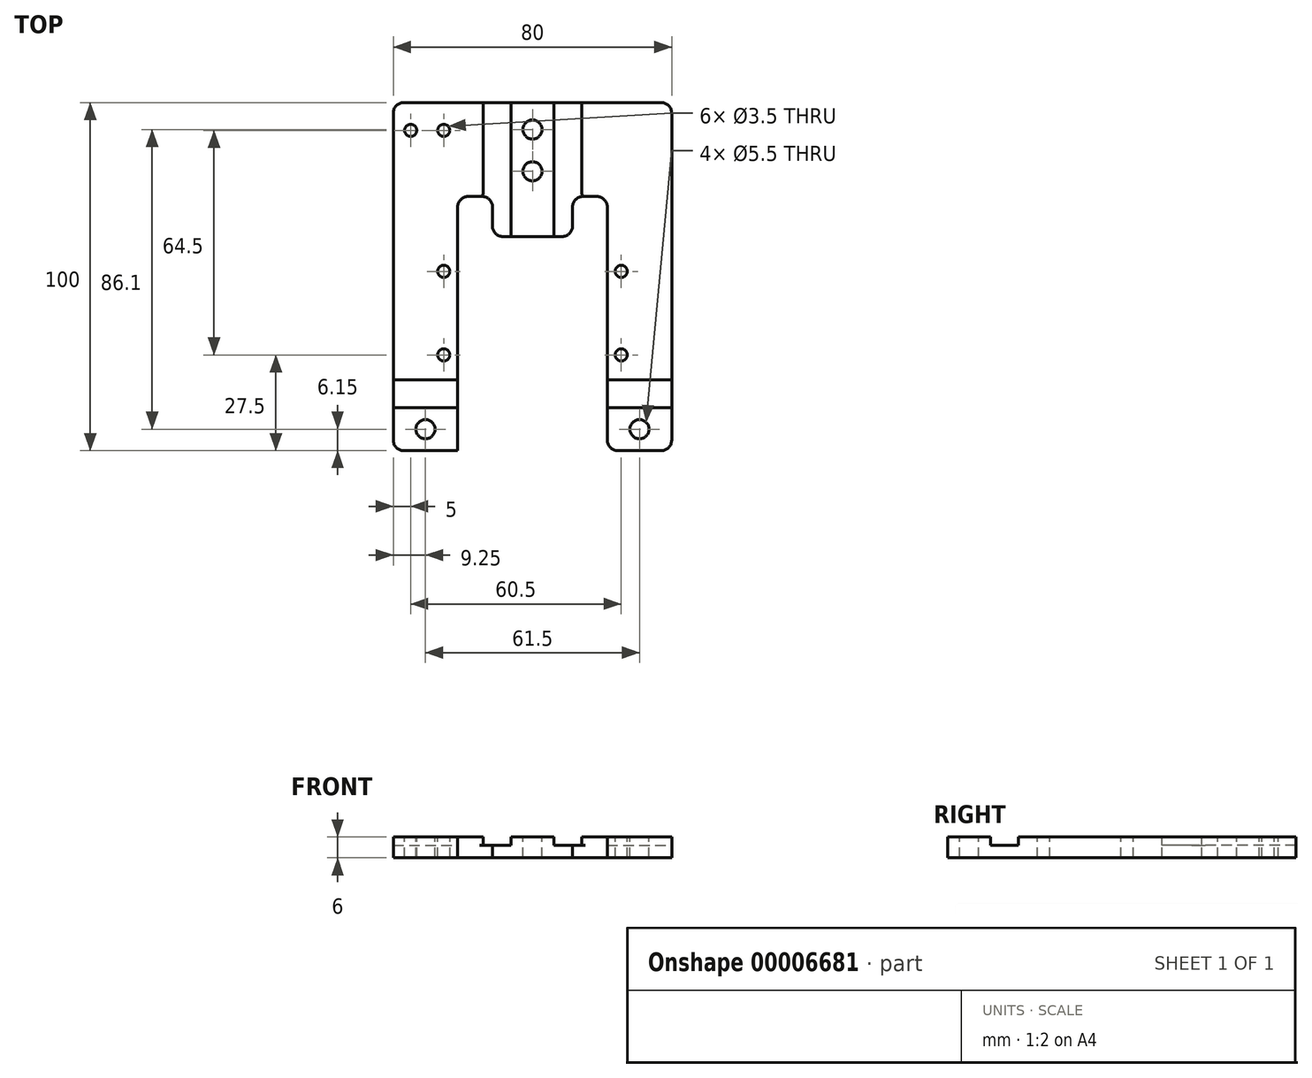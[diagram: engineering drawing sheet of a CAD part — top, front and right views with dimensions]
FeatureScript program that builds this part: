
annotation { "Feature Type Name" : "Feature", "Feature Type Description" : "" }
export const myFeature = defineFeature(function(context is Context, id is Id, definition is map)
    precondition{}
    {
        {
            var Q0;
            Q0=qCreatedBy(makeId("Top.planeOp"),FACE);
            var sketch = newSketch(context, id + "F0", { "sketchPlane" : qUnion([Q0])});
            skLineSegment(sketch, "E0.bottom", {"start": v(0, 0) * mm, "end": v(80, 0) * mm});
            skLineSegment(sketch, "E0.top", {"start": v(0, 100) * mm, "end": v(80, 100) * mm});
            skLineSegment(sketch, "E0.left", {"start": v(0, 0) * mm, "end": v(0, 100) * mm});
            skLineSegment(sketch, "E0.right", {"start": v(80, 0) * mm, "end": v(80, 100) * mm});
            skSolve(sketch);
        }
        {
            var Q0;
            Q0 = qSketchRegion(id + "F0", true);
            extrude(context, id + "F1", {"entities" : qUnion([Q0]), "depth" : 6 * mm});
        }
        {
            var Q0;
            Q0=makeQuery(id+"F1.opExtrude","CAP_FACE",FACE,{"disambiguationData":[OSD([sQuery(id+"F0.wireOp",EDGE,"E0.bottom"),sQuery(id+"F0.wireOp",EDGE,"E0.top"),sQuery(id+"F0.wireOp",EDGE,"E0.left"),sQuery(id+"F0.wireOp",EDGE,"E0.right")])],"isStart":false});
            var sketch = newSketch(context, id + "F2", { "sketchPlane" : qUnion([Q0])});
            skLineSegment(sketch, "E1.bottom", {"start": v(18.5, 0) * mm, "end": v(61.5, 0) * mm});
            skLineSegment(sketch, "E1.top", {"start": v(28.5, 61.5) * mm, "end": v(51.5, 61.5) * mm});
            skLineSegment(sketch, "E1.left", {"start": v(18.5, 0) * mm, "end": v(18.5, 61.5) * mm});
            skLineSegment(sketch, "E1.right", {"start": v(61.5, 0) * mm, "end": v(61.5, 61.5) * mm});
            skLineSegment(sketch, "E2.top", {"start": v(18.5, 73) * mm, "end": v(28.5, 73) * mm});
            skLineSegment(sketch, "E2.left", {"start": v(18.5, 61.5) * mm, "end": v(18.5, 73) * mm});
            skLineSegment(sketch, "E2.right", {"start": v(28.5, 61.5) * mm, "end": v(28.5, 73) * mm});
            skLineSegment(sketch, "E3.top", {"start": v(61.5, 73) * mm, "end": v(51.5, 73) * mm});
            skLineSegment(sketch, "E3.left", {"start": v(61.5, 61.5) * mm, "end": v(61.5, 73) * mm});
            skLineSegment(sketch, "E3.right", {"start": v(51.5, 61.5) * mm, "end": v(51.5, 73) * mm});
            skSolve(sketch);
        }
        {
            var Q0;
            Q0 = qSketchRegion(id + "F2", true);
            extrude(context, id + "F3", {"entities" : qUnion([Q0]), "operationType" : NewBodyOperationType.REMOVE, "endBound" : BoundingType.THROUGH_ALL, "oppositeDirection" : true, "depth" : 25 * mm});
        }
        {
            var Q0;
            Q0=makeQuery(id+"F1.opExtrude","CAP_FACE",FACE,{"disambiguationData":[OSD([sQuery(id+"F0.wireOp",EDGE,"E0.bottom"),sQuery(id+"F0.wireOp",EDGE,"E0.top"),sQuery(id+"F0.wireOp",EDGE,"E0.left"),sQuery(id+"F0.wireOp",EDGE,"E0.right")])],"isStart":false});
            var sketch = newSketch(context, id + "F4", { "sketchPlane" : qUnion([Q0])});
            skLineSegment(sketch, "E4", {"start": v(0, 12.3) * mm, "end": v(18.5, 12.3) * mm});
            skLineSegment(sketch, "E5", {"start": v(61.5, 12.3) * mm, "end": v(80, 12.3) * mm});
            skLineSegment(sketch, "E6.0", {"start": v(46.15, 100) * mm, "end": v(46.15, 61.5) * mm});
            skLineSegment(sketch, "E7.0", {"start": v(33.85, 100) * mm, "end": v(33.85, 61.5) * mm});
            skLineSegment(sketch, "E8.0", {"start": v(25.85, 100) * mm, "end": v(25.85, 61.5) * mm});
            skLineSegment(sketch, "E9.0", {"start": v(54.15, 100) * mm, "end": v(54.15, 61.5) * mm});
            skLineSegment(sketch, "E10.0", {"start": v(61.5, 20.3) * mm, "end": v(80, 20.3) * mm});
            skLineSegment(sketch, "E11.0", {"start": v(0, 20.3) * mm, "end": v(18.5, 20.3) * mm});
            skLineSegment(sketch, "E12", {"start": v(25.85, 100) * mm, "end": v(33.85, 100) * mm});
            skLineSegment(sketch, "E13", {"start": v(46.15, 100) * mm, "end": v(54.15, 100) * mm});
            skLineSegment(sketch, "E14", {"start": v(54.15, 61.5) * mm, "end": v(46.15, 61.5) * mm});
            skLineSegment(sketch, "E15", {"start": v(33.85, 61.5) * mm, "end": v(25.85, 61.5) * mm});
            skLineSegment(sketch, "E16", {"start": v(0, 20.3) * mm, "end": v(0, 12.3) * mm});
            skLineSegment(sketch, "E17", {"start": v(18.5, 12.3) * mm, "end": v(18.5, 20.3) * mm});
            skLineSegment(sketch, "E18", {"start": v(61.5, 20.3) * mm, "end": v(61.5, 12.3) * mm});
            skLineSegment(sketch, "E19", {"start": v(80, 12.3) * mm, "end": v(80, 20.3) * mm});
            skLineSegment(sketch, "E20", {"start": v(40, 100) * mm, "end": v(40, 61.5) * mm, "construction": true});
            skSolve(sketch);
        }
        {
            var Q0;
            Q0 = qSketchRegion(id + "F4", true);
            extrude(context, id + "F5", {"entities" : qUnion([Q0]), "operationType" : NewBodyOperationType.REMOVE, "oppositeDirection" : true, "depth" : 2.4 * mm});
        }
        {
            var Q0;
            {var subQ0=sQuery(id+"F0.wireOp",EDGE,"E0.top");Q0=makeQuery(id+"F5.boolean.opBoolean","SPLIT",FACE,{"disambiguationData":[TD([makeQuery(id+"F3.boolean.opBoolean","COPY",FACE,{"derivedFrom":makeQuery(id+"F3.opExtrude","SWEPT_FACE",FACE,{"disambiguationData":[OSD([sQuery(id+"F2.wireOp",EDGE,"E1.top")])]})})])],"derivedFrom":makeQuery(id+"F1.opExtrude","CAP_FACE",FACE,{"disambiguationData":[OSD([sQuery(id+"F0.wireOp",EDGE,"E0.bottom"),subQ0,sQuery(id+"F0.wireOp",EDGE,"E0.left"),sQuery(id+"F0.wireOp",EDGE,"E0.right")])],"isStart":false})});}
            var sketch = newSketch(context, id + "F6", { "sketchPlane" : qUnion([Q0])});
            skLineSegment(sketch, "E21", {"start": v(40, 100) * mm, "end": v(40, 61.5) * mm});
            skCircle(sketch, "E22", {"center": v(40, 92.25) * mm, "radius": 2.75 * mm});
            skCircle(sketch, "E23", {"center": v(40, 80.25) * mm, "radius": 2.75 * mm});
            skSolve(sketch);
        }
        {
            var Q0;
            Q0 = qSketchRegion(id + "F6", true);
            extrude(context, id + "F7", {"entities" : qUnion([Q0]), "operationType" : NewBodyOperationType.REMOVE, "endBound" : BoundingType.THROUGH_ALL, "oppositeDirection" : true, "depth" : 25 * mm});
        }
        {
            var Q0;
            {var subQ0=sQuery(id+"F0.wireOp",EDGE,"E0.bottom");var subQ1=sQuery(id+"F0.wireOp",EDGE,"E0.left");Q0=makeQuery(id+"F5.boolean.opBoolean","SPLIT",FACE,{"disambiguationData":[TD([makeQuery(id+"F5.opExtrude","SWEPT_FACE",FACE,{"disambiguationData":[OSD([sQuery(id+"F4.wireOp",EDGE,"E4")])]})])],"derivedFrom":makeQuery(id+"F1.opExtrude","CAP_FACE",FACE,{"disambiguationData":[OSD([subQ0,sQuery(id+"F0.wireOp",EDGE,"E0.top"),subQ1,sQuery(id+"F0.wireOp",EDGE,"E0.right")])],"isStart":false})});}
            var sketch = newSketch(context, id + "F8", { "sketchPlane" : qUnion([Q0])});
            skLineSegment(sketch, "E24", {"start": v(9.25, 12.3) * mm, "end": v(9.25, 0) * mm, "construction": true});
            skCircle(sketch, "E25", {"center": v(9.25, 6.15) * mm, "radius": 2.75 * mm});
            skSolve(sketch);
        }
        {
            var Q0;
            Q0 = qSketchRegion(id + "F8", true);
            extrude(context, id + "F9", {"entities" : qUnion([Q0]), "operationType" : NewBodyOperationType.REMOVE, "endBound" : BoundingType.THROUGH_ALL, "oppositeDirection" : true, "depth" : 25 * mm});
        }
        {
            var Q0;
            {var subQ0=sQuery(id+"F0.wireOp",EDGE,"E0.bottom");var subQ1=sQuery(id+"F0.wireOp",EDGE,"E0.right");Q0=makeQuery(id+"F5.boolean.opBoolean","SPLIT",FACE,{"disambiguationData":[TD([makeQuery(id+"F5.opExtrude","SWEPT_FACE",FACE,{"disambiguationData":[OSD([sQuery(id+"F4.wireOp",EDGE,"E5")])]})])],"derivedFrom":makeQuery(id+"F1.opExtrude","CAP_FACE",FACE,{"disambiguationData":[OSD([subQ0,sQuery(id+"F0.wireOp",EDGE,"E0.top"),sQuery(id+"F0.wireOp",EDGE,"E0.left"),subQ1])],"isStart":false})});}
            var sketch = newSketch(context, id + "F10", { "sketchPlane" : qUnion([Q0])});
            skLineSegment(sketch, "E26", {"start": v(70.75, 12.3) * mm, "end": v(70.75, 0) * mm, "construction": true});
            skCircle(sketch, "E27", {"center": v(70.75, 6.15) * mm, "radius": 2.75 * mm});
            skSolve(sketch);
        }
        {
            var Q0;
            Q0 = qSketchRegion(id + "F10", true);
            extrude(context, id + "F11", {"entities" : qUnion([Q0]), "operationType" : NewBodyOperationType.REMOVE, "endBound" : BoundingType.THROUGH_ALL, "oppositeDirection" : true, "depth" : 25 * mm});
        }
        {
            var Q0;
            {var subQ0=sQuery(id+"F0.wireOp",EDGE,"E0.top");var subQ1=sQuery(id+"F0.wireOp",EDGE,"E0.left");Q0=makeQuery(id+"F5.boolean.opBoolean","SPLIT",FACE,{"disambiguationData":[TD([makeQuery(id+"F3.boolean.opBoolean","COPY",FACE,{"derivedFrom":makeQuery(id+"F3.opExtrude","SWEPT_FACE",FACE,{"disambiguationData":[OSD([sQuery(id+"F2.wireOp",EDGE,"E2.top")])]})})])],"derivedFrom":makeQuery(id+"F1.opExtrude","CAP_FACE",FACE,{"disambiguationData":[OSD([sQuery(id+"F0.wireOp",EDGE,"E0.bottom"),subQ0,subQ1,sQuery(id+"F0.wireOp",EDGE,"E0.right")])],"isStart":false})});}
            var sketch = newSketch(context, id + "F12", { "sketchPlane" : qUnion([Q0])});
            skLineSegment(sketch, "E28", {"start": v(0, 92) * mm, "end": v(25.85, 92) * mm, "construction": true});
            skCircle(sketch, "E29", {"center": v(5, 92) * mm, "radius": 1.75 * mm});
            skCircle(sketch, "E30", {"center": v(14.5, 92) * mm, "radius": 1.75 * mm});
            skSolve(sketch);
        }
        {
            var Q0;
            Q0 = qSketchRegion(id + "F12", true);
            extrude(context, id + "F13", {"entities" : qUnion([Q0]), "operationType" : NewBodyOperationType.REMOVE, "endBound" : BoundingType.THROUGH_ALL, "oppositeDirection" : true, "depth" : 25 * mm});
        }
        {
            var Q0;
            {var subQ0=sQuery(id+"F0.wireOp",EDGE,"E0.top");var subQ1=sQuery(id+"F0.wireOp",EDGE,"E0.left");Q0=makeQuery(id+"F5.boolean.opBoolean","SPLIT",FACE,{"disambiguationData":[TD([makeQuery(id+"F3.boolean.opBoolean","COPY",FACE,{"derivedFrom":makeQuery(id+"F3.opExtrude","SWEPT_FACE",FACE,{"disambiguationData":[OSD([sQuery(id+"F2.wireOp",EDGE,"E2.top")])]})})])],"derivedFrom":makeQuery(id+"F1.opExtrude","CAP_FACE",FACE,{"disambiguationData":[OSD([sQuery(id+"F0.wireOp",EDGE,"E0.bottom"),subQ0,subQ1,sQuery(id+"F0.wireOp",EDGE,"E0.right")])],"isStart":false})});}
            var sketch = newSketch(context, id + "F14", { "sketchPlane" : qUnion([Q0])});
            skLineSegment(sketch, "E31", {"start": v(14.5, 20.3) * mm, "end": v(14.5, 73) * mm, "construction": true});
            skCircle(sketch, "E32", {"center": v(14.5, 51.5) * mm, "radius": 1.75 * mm});
            skCircle(sketch, "E33", {"center": v(14.5, 27.5) * mm, "radius": 1.75 * mm});
            skSolve(sketch);
        }
        {
            var Q0;
            Q0 = qSketchRegion(id + "F14", true);
            extrude(context, id + "F15", {"entities" : qUnion([Q0]), "operationType" : NewBodyOperationType.REMOVE, "endBound" : BoundingType.THROUGH_ALL, "oppositeDirection" : true, "depth" : 25 * mm});
        }
        {
            var Q0;
            {var subQ0=sQuery(id+"F0.wireOp",EDGE,"E0.top");var subQ1=sQuery(id+"F0.wireOp",EDGE,"E0.right");Q0=makeQuery(id+"F5.boolean.opBoolean","SPLIT",FACE,{"disambiguationData":[TD([makeQuery(id+"F3.boolean.opBoolean","COPY",FACE,{"derivedFrom":makeQuery(id+"F3.opExtrude","SWEPT_FACE",FACE,{"disambiguationData":[OSD([sQuery(id+"F2.wireOp",EDGE,"E3.top")])]})})])],"derivedFrom":makeQuery(id+"F1.opExtrude","CAP_FACE",FACE,{"disambiguationData":[OSD([sQuery(id+"F0.wireOp",EDGE,"E0.bottom"),subQ0,sQuery(id+"F0.wireOp",EDGE,"E0.left"),subQ1])],"isStart":false})});}
            var sketch = newSketch(context, id + "F16", { "sketchPlane" : qUnion([Q0])});
            skLineSegment(sketch, "E34", {"start": v(65.5, 20.3) * mm, "end": v(65.5, 51.38) * mm, "construction": true});
            skCircle(sketch, "E35", {"center": v(65.5, 51.5) * mm, "radius": 1.75 * mm});
            skCircle(sketch, "E36", {"center": v(65.5, 27.5) * mm, "radius": 1.75 * mm});
            skSolve(sketch);
        }
        {
            var Q0;
            Q0 = qSketchRegion(id + "F16", true);
            extrude(context, id + "F17", {"entities" : qUnion([Q0]), "operationType" : NewBodyOperationType.REMOVE, "endBound" : BoundingType.THROUGH_ALL, "oppositeDirection" : true, "depth" : 25 * mm});
        }
        {
            var Q0;
            Q0=makeQuery(id+"F1.opExtrude","SWEPT_EDGE",EDGE,{"disambiguationData":[OSD([sQuery(id+"F0.wireOp",EDGE,"E0.bottom"),sQuery(id+"F0.wireOp",EDGE,"E0.left")])]});
            var Q1;
            Q1=makeQuery(id+"F1.opExtrude","SWEPT_EDGE",EDGE,{"disambiguationData":[OSD([sQuery(id+"F0.wireOp",EDGE,"E0.bottom"),sQuery(id+"F0.wireOp",EDGE,"E0.right")])]});
            var Q2;
            Q2=makeQuery(id+"F3.boolean.opBoolean","COPY",EDGE,{"derivedFrom":makeQuery(id+"F3.opExtrude","SWEPT_EDGE",EDGE,{"disambiguationData":[OSD([sQuery(id+"F0.wireOp",EDGE,"E0.bottom"),sQuery(id+"F2.wireOp",EDGE,"E1.bottom"),sQuery(id+"F2.wireOp",EDGE,"E1.right")])]})});
            var Q3;
            Q3=makeQuery(id+"F3.boolean.opBoolean","COPY",EDGE,{"derivedFrom":makeQuery(id+"F3.opExtrude","SWEPT_EDGE",EDGE,{"disambiguationData":[OSD([sQuery(id+"F0.wireOp",EDGE,"E0.bottom"),sQuery(id+"F2.wireOp",EDGE,"E1.bottom"),sQuery(id+"F2.wireOp",EDGE,"E1.left")])]})});
            var Q4;
            Q4=makeQuery(id+"F1.opExtrude","SWEPT_EDGE",EDGE,{"disambiguationData":[OSD([sQuery(id+"F0.wireOp",EDGE,"E0.top"),sQuery(id+"F0.wireOp",EDGE,"E0.left")])]});
            var Q5;
            Q5=makeQuery(id+"F1.opExtrude","SWEPT_EDGE",EDGE,{"disambiguationData":[OSD([sQuery(id+"F0.wireOp",EDGE,"E0.top"),sQuery(id+"F0.wireOp",EDGE,"E0.right")])]});
            var Q6;
            Q6=makeQuery(id+"F3.boolean.opBoolean","COPY",EDGE,{"derivedFrom":makeQuery(id+"F3.opExtrude","SWEPT_EDGE",EDGE,{"disambiguationData":[OSD([sQuery(id+"F2.wireOp",EDGE,"E1.top"),sQuery(id+"F2.wireOp",EDGE,"E3.right")])]})});
            var Q7;
            Q7=makeQuery(id+"F3.boolean.opBoolean","COPY",EDGE,{"derivedFrom":makeQuery(id+"F3.opExtrude","SWEPT_EDGE",EDGE,{"disambiguationData":[OSD([sQuery(id+"F2.wireOp",EDGE,"E1.top"),sQuery(id+"F2.wireOp",EDGE,"E2.right")])]})});
            var Q8;
            Q8=makeQuery(id+"F3.boolean.opBoolean","COPY",EDGE,{"derivedFrom":makeQuery(id+"F3.opExtrude","SWEPT_EDGE",EDGE,{"disambiguationData":[OSD([sQuery(id+"F2.wireOp",EDGE,"E3.top"),sQuery(id+"F2.wireOp",EDGE,"E3.left")])]})});
            var Q9;
            Q9=makeQuery(id+"F3.boolean.opBoolean","COPY",EDGE,{"derivedFrom":makeQuery(id+"F3.opExtrude","SWEPT_EDGE",EDGE,{"disambiguationData":[OSD([sQuery(id+"F2.wireOp",EDGE,"E2.top"),sQuery(id+"F2.wireOp",EDGE,"E2.left")])]})});
            var Q10;
            Q10=makeQuery(id+"F3.boolean.opBoolean","COPY",EDGE,{"derivedFrom":makeQuery(id+"F3.opExtrude","SWEPT_EDGE",EDGE,{"disambiguationData":[OSD([sQuery(id+"F2.wireOp",EDGE,"E3.top"),sQuery(id+"F2.wireOp",EDGE,"E3.right")])]})});
            var Q11;
            Q11=makeQuery(id+"F3.boolean.opBoolean","COPY",EDGE,{"derivedFrom":makeQuery(id+"F3.opExtrude","SWEPT_EDGE",EDGE,{"disambiguationData":[OSD([sQuery(id+"F2.wireOp",EDGE,"E2.top"),sQuery(id+"F2.wireOp",EDGE,"E2.right")])]})});
            fillet(context, id + "F18", {"entities" : qUnion([Q0, Q1, Q2, Q3, Q4, Q5, Q6, Q7, Q8, Q9, Q10, Q11]), "radius" : 3 * mm, "tangentPropagation" : true, "allowEdgeOverflow" : false});
        }
        {
            var Q0;
            Q0=makeQuery(id+"F5.boolean.opBoolean","COPY",EDGE,{"derivedFrom":makeQuery(id+"F5.opExtrude","SWEPT_EDGE",EDGE,{"disambiguationData":[OSD([sQuery(id+"F2.wireOp",EDGE,"E1.top"),sQuery(id+"F4.wireOp",EDGE,"E7.0"),sQuery(id+"F4.wireOp",EDGE,"E15")])]})});
            var Q1;
            Q1=makeQuery(id+"F18.opFillet","BLEND_EDGE",EDGE,{"blendedFrom":[makeQuery(id+"F3.boolean.opBoolean","COPY",EDGE,{"derivedFrom":makeQuery(id+"F3.opExtrude","SWEPT_EDGE",EDGE,{"disambiguationData":[OSD([sQuery(id+"F2.wireOp",EDGE,"E3.top"),sQuery(id+"F2.wireOp",EDGE,"E3.right")])]})}),makeQuery(id+"F5.boolean.opBoolean","COPY",FACE,{"derivedFrom":makeQuery(id+"F5.opExtrude","SWEPT_FACE",FACE,{"disambiguationData":[OSD([sQuery(id+"F4.wireOp",EDGE,"E9.0")])]})})],"blendedInto":[makeQuery(id+"F5.boolean.opBoolean","COPY",FACE,{"derivedFrom":makeQuery(id+"F5.opExtrude","SWEPT_FACE",FACE,{"disambiguationData":[OSD([sQuery(id+"F4.wireOp",EDGE,"E9.0")])]})})]});
            var Q2;
            Q2=makeQuery(id+"F5.boolean.opBoolean","COPY",EDGE,{"derivedFrom":makeQuery(id+"F5.opExtrude","SWEPT_EDGE",EDGE,{"disambiguationData":[OSD([sQuery(id+"F2.wireOp",EDGE,"E1.top"),sQuery(id+"F4.wireOp",EDGE,"E6.0"),sQuery(id+"F4.wireOp",EDGE,"E14")])]})});
            var Q3;
            Q3=makeQuery(id+"F18.opFillet","BLEND_EDGE",EDGE,{"blendedFrom":[makeQuery(id+"F3.boolean.opBoolean","COPY",EDGE,{"derivedFrom":makeQuery(id+"F3.opExtrude","SWEPT_EDGE",EDGE,{"disambiguationData":[OSD([sQuery(id+"F2.wireOp",EDGE,"E2.top"),sQuery(id+"F2.wireOp",EDGE,"E2.right")])]})}),makeQuery(id+"F5.boolean.opBoolean","COPY",FACE,{"derivedFrom":makeQuery(id+"F5.opExtrude","SWEPT_FACE",FACE,{"disambiguationData":[OSD([sQuery(id+"F4.wireOp",EDGE,"E8.0")])]})})],"blendedInto":[makeQuery(id+"F5.boolean.opBoolean","COPY",FACE,{"derivedFrom":makeQuery(id+"F5.opExtrude","SWEPT_FACE",FACE,{"disambiguationData":[OSD([sQuery(id+"F4.wireOp",EDGE,"E8.0")])]})})]});
            var Q4;
            Q4=makeQuery(id+"F5.boolean.opBoolean","COPY",EDGE,{"derivedFrom":makeQuery(id+"F5.opExtrude","SWEPT_EDGE",EDGE,{"disambiguationData":[OSD([sQuery(id+"F0.wireOp",EDGE,"E0.top"),sQuery(id+"F4.wireOp",EDGE,"E8.0"),sQuery(id+"F4.wireOp",EDGE,"E12")])]})});
            var Q5;
            Q5=makeQuery(id+"F5.boolean.opBoolean","COPY",EDGE,{"derivedFrom":makeQuery(id+"F5.opExtrude","SWEPT_EDGE",EDGE,{"disambiguationData":[OSD([sQuery(id+"F0.wireOp",EDGE,"E0.top"),sQuery(id+"F4.wireOp",EDGE,"E7.0"),sQuery(id+"F4.wireOp",EDGE,"E12")])]})});
            var Q6;
            Q6=makeQuery(id+"F5.boolean.opBoolean","COPY",EDGE,{"derivedFrom":makeQuery(id+"F5.opExtrude","SWEPT_EDGE",EDGE,{"disambiguationData":[OSD([sQuery(id+"F0.wireOp",EDGE,"E0.top"),sQuery(id+"F4.wireOp",EDGE,"E6.0"),sQuery(id+"F4.wireOp",EDGE,"E13")])]})});
            var Q7;
            Q7=makeQuery(id+"F5.boolean.opBoolean","COPY",EDGE,{"derivedFrom":makeQuery(id+"F5.opExtrude","SWEPT_EDGE",EDGE,{"disambiguationData":[OSD([sQuery(id+"F0.wireOp",EDGE,"E0.top"),sQuery(id+"F4.wireOp",EDGE,"E9.0"),sQuery(id+"F4.wireOp",EDGE,"E13")])]})});
            var Q8;
            Q8=makeQuery(id+"F5.boolean.opBoolean","COPY",EDGE,{"derivedFrom":makeQuery(id+"F5.opExtrude","SWEPT_EDGE",EDGE,{"disambiguationData":[OSD([sQuery(id+"F2.wireOp",EDGE,"E1.left"),sQuery(id+"F2.wireOp",EDGE,"E2.left"),sQuery(id+"F4.wireOp",EDGE,"E4"),sQuery(id+"F4.wireOp",EDGE,"E17")])]})});
            var Q9;
            Q9=makeQuery(id+"F5.boolean.opBoolean","COPY",EDGE,{"derivedFrom":makeQuery(id+"F5.opExtrude","SWEPT_EDGE",EDGE,{"disambiguationData":[OSD([sQuery(id+"F0.wireOp",EDGE,"E0.left"),sQuery(id+"F4.wireOp",EDGE,"E4"),sQuery(id+"F4.wireOp",EDGE,"E16")])]})});
            var Q10;
            Q10=makeQuery(id+"F5.boolean.opBoolean","COPY",EDGE,{"derivedFrom":makeQuery(id+"F5.opExtrude","SWEPT_EDGE",EDGE,{"disambiguationData":[OSD([sQuery(id+"F2.wireOp",EDGE,"E1.left"),sQuery(id+"F2.wireOp",EDGE,"E2.left"),sQuery(id+"F4.wireOp",EDGE,"E11.0"),sQuery(id+"F4.wireOp",EDGE,"E17")])]})});
            var Q11;
            Q11=makeQuery(id+"F5.boolean.opBoolean","COPY",EDGE,{"derivedFrom":makeQuery(id+"F5.opExtrude","SWEPT_EDGE",EDGE,{"disambiguationData":[OSD([sQuery(id+"F0.wireOp",EDGE,"E0.right"),sQuery(id+"F4.wireOp",EDGE,"E5"),sQuery(id+"F4.wireOp",EDGE,"E19")])]})});
            var Q12;
            Q12=makeQuery(id+"F5.boolean.opBoolean","COPY",EDGE,{"derivedFrom":makeQuery(id+"F5.opExtrude","SWEPT_EDGE",EDGE,{"disambiguationData":[OSD([sQuery(id+"F0.wireOp",EDGE,"E0.right"),sQuery(id+"F4.wireOp",EDGE,"E10.0"),sQuery(id+"F4.wireOp",EDGE,"E19")])]})});
            var Q13;
            Q13=makeQuery(id+"F5.boolean.opBoolean","COPY",EDGE,{"derivedFrom":makeQuery(id+"F5.opExtrude","SWEPT_EDGE",EDGE,{"disambiguationData":[OSD([sQuery(id+"F2.wireOp",EDGE,"E1.right"),sQuery(id+"F2.wireOp",EDGE,"E3.left"),sQuery(id+"F4.wireOp",EDGE,"E5"),sQuery(id+"F4.wireOp",EDGE,"E18")])]})});
            var Q14;
            Q14=makeQuery(id+"F5.boolean.opBoolean","COPY",EDGE,{"derivedFrom":makeQuery(id+"F5.opExtrude","SWEPT_EDGE",EDGE,{"disambiguationData":[OSD([sQuery(id+"F2.wireOp",EDGE,"E1.right"),sQuery(id+"F2.wireOp",EDGE,"E3.left"),sQuery(id+"F4.wireOp",EDGE,"E10.0"),sQuery(id+"F4.wireOp",EDGE,"E18")])]})});
            var Q15;
            Q15=makeQuery(id+"F5.boolean.opBoolean","COPY",EDGE,{"derivedFrom":makeQuery(id+"F5.opExtrude","SWEPT_EDGE",EDGE,{"disambiguationData":[OSD([sQuery(id+"F0.wireOp",EDGE,"E0.left"),sQuery(id+"F4.wireOp",EDGE,"E11.0"),sQuery(id+"F4.wireOp",EDGE,"E16")])]})});
            fillet(context, id + "F19", {"entities" : qUnion([Q0, Q1, Q2, Q3, Q4, Q5, Q6, Q7, Q8, Q9, Q10, Q11, Q12, Q13, Q14, Q15]), "radius" : 1 * mm, "tangentPropagation" : true, "allowEdgeOverflow" : false});
        }
    });
